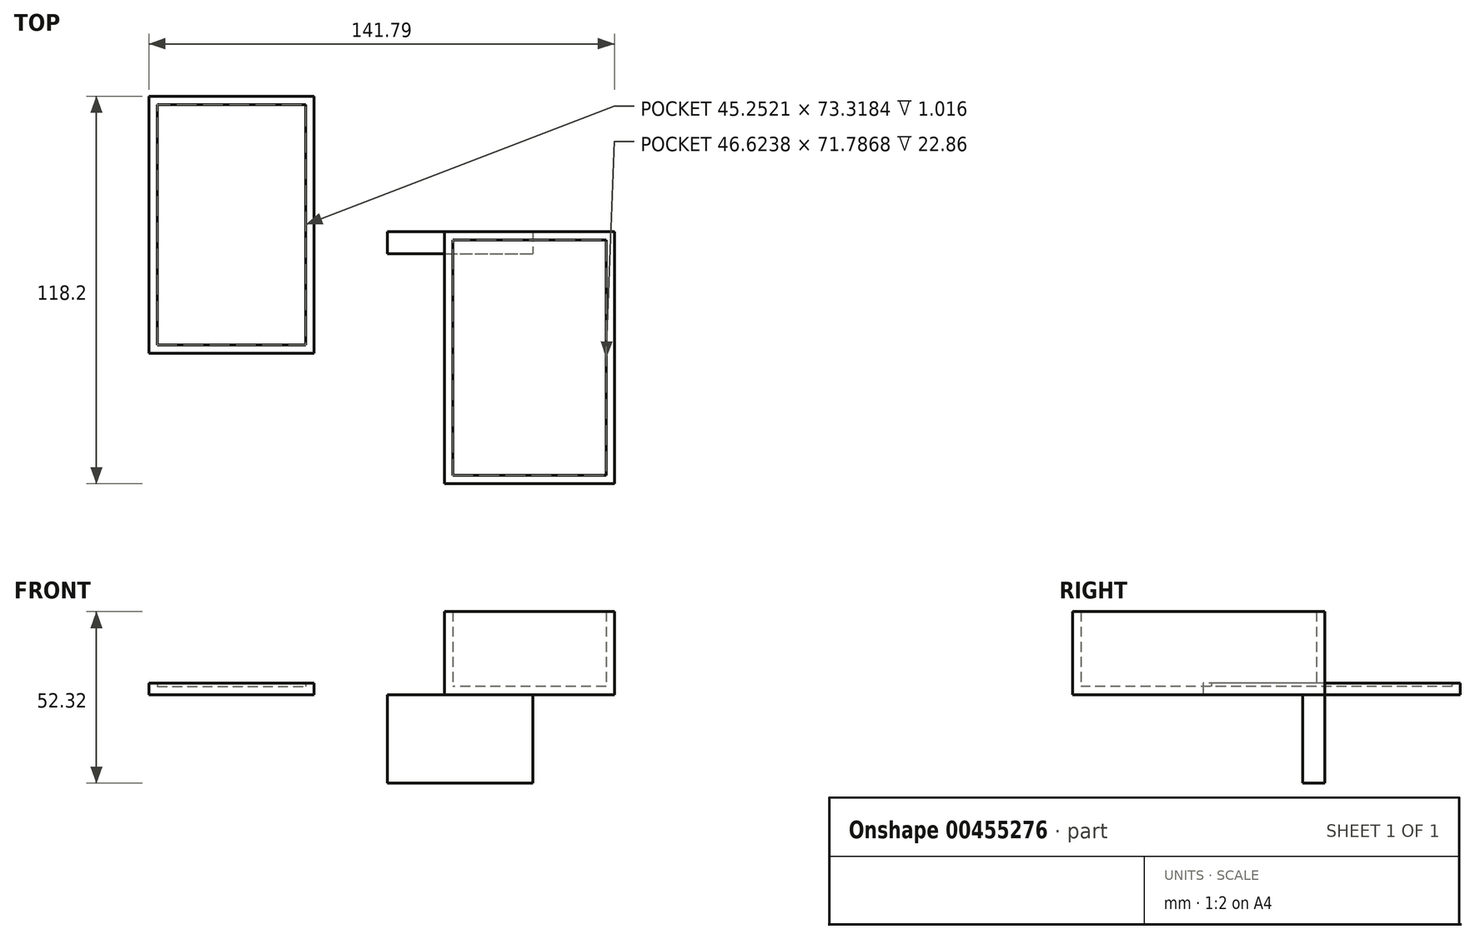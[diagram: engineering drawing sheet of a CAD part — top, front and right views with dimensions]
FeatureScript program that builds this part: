
annotation { "Feature Type Name" : "Feature", "Feature Type Description" : "" }
export const myFeature = defineFeature(function(context is Context, id is Id, definition is map)
    precondition{}
    {
        {
            var Q0;
            Q0=qCreatedBy(makeId("Top.planeOp"),FACE);
            var sketch = newSketch(context, id + "F0", { "sketchPlane" : qUnion([Q0])});
            skLineSegment(sketch, "E0.bottom", {"start": v(0, 0) * mm, "end": v(-51.7, 0) * mm});
            skLineSegment(sketch, "E0.top", {"start": v(0, -76.87) * mm, "end": v(-51.7, -76.87) * mm});
            skLineSegment(sketch, "E0.left", {"start": v(0, 0) * mm, "end": v(0, -76.87) * mm});
            skLineSegment(sketch, "E0.right", {"start": v(-51.7, 0) * mm, "end": v(-51.7, -76.87) * mm});
            skSolve(sketch);
        }
        {
            var Q0;
            Q0 = qSketchRegion(id + "F0", true);
            extrude(context, id + "F1", {"entities" : qUnion([Q0]), "depth" : 25.4 * mm});
        }
        {
            var Q0;
            Q0=makeQuery(id+"F1.opExtrude","CAP_FACE",FACE,{"disambiguationData":[OSD([sQuery(id+"F0.wireOp",EDGE,"E0.bottom"),sQuery(id+"F0.wireOp",EDGE,"E0.top"),sQuery(id+"F0.wireOp",EDGE,"E0.left"),sQuery(id+"F0.wireOp",EDGE,"E0.right")])],"isStart":false});
            shell(context, id + "F2", {"entities" : qUnion([Q0]), "thickness" : 2.54 * mm});
        }
        {
            var Q0;
            Q0=qCreatedBy(makeId("Top.planeOp"),FACE);
            var sketch = newSketch(context, id + "F3", { "sketchPlane" : qUnion([Q0])});
            skLineSegment(sketch, "E1.bottom", {"start": v(-141.8, 41.33) * mm, "end": v(-91.46, 41.33) * mm});
            skLineSegment(sketch, "E1.top", {"start": v(-141.8, -37.07) * mm, "end": v(-91.46, -37.07) * mm});
            skLineSegment(sketch, "E1.left", {"start": v(-141.8, 41.33) * mm, "end": v(-141.8, -37.07) * mm});
            skLineSegment(sketch, "E1.right", {"start": v(-91.46, 41.33) * mm, "end": v(-91.46, -37.07) * mm});
            skSolve(sketch);
        }
        {
            var Q0;
            Q0 = qSketchRegion(id + "F3", true);
            extrude(context, id + "F4", {"entities" : qUnion([Q0]), "depth" : 3.56 * mm});
        }
        {
            var Q0;
            Q0=makeQuery(id+"F4.opExtrude","CAP_FACE",FACE,{"disambiguationData":[OSD([sQuery(id+"F3.wireOp",EDGE,"E1.bottom"),sQuery(id+"F3.wireOp",EDGE,"E1.top"),sQuery(id+"F3.wireOp",EDGE,"E1.left"),sQuery(id+"F3.wireOp",EDGE,"E1.right")])],"isStart":false});
            shell(context, id + "F5", {"entities" : qUnion([Q0]), "thickness" : 2.54 * mm});
        }
        {
            var Q0;
            Q0=qCreatedBy(makeId("Top.planeOp"),FACE);
            var sketch = newSketch(context, id + "F6", { "sketchPlane" : qUnion([Q0])});
            skLineSegment(sketch, "E2.bottom", {"start": v(-69.19, 0) * mm, "end": v(-24.84, 0) * mm});
            skLineSegment(sketch, "E2.top", {"start": v(-69.19, -6.72) * mm, "end": v(-24.84, -6.72) * mm});
            skLineSegment(sketch, "E2.left", {"start": v(-69.19, 0) * mm, "end": v(-69.19, -6.72) * mm});
            skLineSegment(sketch, "E2.right", {"start": v(-24.84, 0) * mm, "end": v(-24.84, -6.72) * mm});
            skSolve(sketch);
        }
        {
            var Q0;
            Q0 = qSketchRegion(id + "F6", true);
            extrude(context, id + "F7", {"entities" : qUnion([Q0]), "operationType" : NewBodyOperationType.ADD, "oppositeDirection" : true, "depth" : 26.92 * mm});
        }
    });
